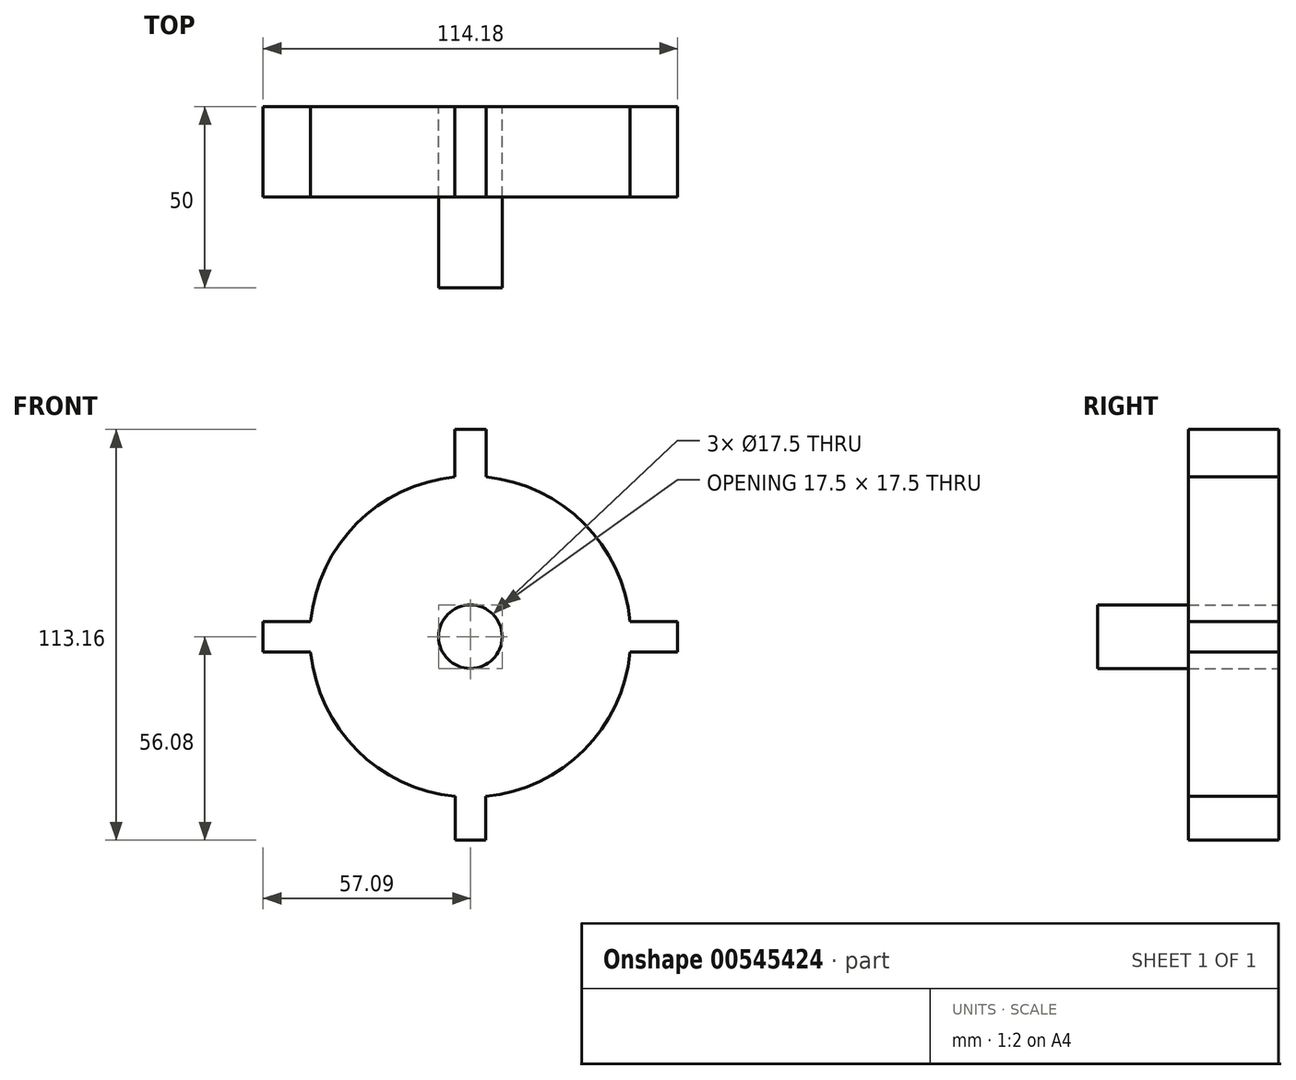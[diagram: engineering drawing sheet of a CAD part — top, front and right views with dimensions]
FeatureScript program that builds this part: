
annotation { "Feature Type Name" : "Feature", "Feature Type Description" : "" }
export const myFeature = defineFeature(function(context is Context, id is Id, definition is map)
    precondition{}
    {
        {
            var Q0;
            Q0=qCreatedBy(makeId("Front.planeOp"),FACE);
            var sketch = newSketch(context, id + "F0", { "sketchPlane" : qUnion([Q0])});
            skLineSegment(sketch, "E0.top", {"start": v(4.3, 57.08) * mm, "end": v(-4.3, 57.08) * mm});
            skLineSegment(sketch, "E0.left", {"start": v(4.3, 44) * mm, "end": v(4.3, 57.08) * mm});
            skLineSegment(sketch, "E0.right", {"start": v(-4.3, 44) * mm, "end": v(-4.3, 57.08) * mm});
            skPoint(sketch, "E0.middle", {"position": v(0, 50.54) * mm});
            skLineSegment(sketch, "E1.1.1", {"start": v(-44, -4.2) * mm, "end": v(-57.09, -4.2) * mm});
            skLineSegment(sketch, "E1.1.2", {"start": v(-57.09, 4.2) * mm, "end": v(-57.09, -4.2) * mm});
            skLineSegment(sketch, "E1.1.3", {"start": v(-44, 4.2) * mm, "end": v(-57.09, 4.2) * mm});
            skLineSegment(sketch, "E1.2.1", {"start": v(4.2, -43) * mm, "end": v(4.2, -56.08) * mm});
            skLineSegment(sketch, "E1.2.2", {"start": v(-4.2, -56.08) * mm, "end": v(4.2, -56.08) * mm});
            skLineSegment(sketch, "E1.2.3", {"start": v(-4.2, -43) * mm, "end": v(-4.2, -56.08) * mm});
            skLineSegment(sketch, "E1.3.1", {"start": v(44, 4.2) * mm, "end": v(57.09, 4.2) * mm});
            skLineSegment(sketch, "E1.3.2", {"start": v(57.09, -4.2) * mm, "end": v(57.09, 4.2) * mm});
            skLineSegment(sketch, "E1.3.3", {"start": v(44, -4.2) * mm, "end": v(57.09, -4.2) * mm});
            skPoint(sketch, "E1.center", {"position": v(0, 0) * mm});
            skArc(sketch, "E2", {"start": v(-4.3, 44) * mm, "mid": v(-31.3, 31.23) * mm, "end": v(-44, 4.2) * mm});
            skArc(sketch, "E3.trimOffspring", {"start": v(44, 4.2) * mm, "mid": v(31.3, 31.23) * mm, "end": v(4.3, 44) * mm});
            skArc(sketch, "E4.trimOffspring", {"start": v(4.2, -44) * mm, "mid": v(31.26, -31.26) * mm, "end": v(44, -4.2) * mm});
            skArc(sketch, "E5.trimOffspring", {"start": v(-44, -4.2) * mm, "mid": v(-31.26, -31.26) * mm, "end": v(-4.2, -44) * mm});
            skSolve(sketch);
        }
        {
            var Q0;
            Q0=makeQuery(id+"F0.imprint","IMPRINT",FACE,{"disambiguationData":[TD([[makeQuery(id+"F0.imprint","IMPRINT",EDGE,{"derivedFrom":sQuery(id+"F0.wireOp",EDGE,"E0.top")}),1.0]])]});
            extrude(context, id + "F1", {"entities" : qUnion([Q0]), "depth" : 25 * mm, "offsetDistance" : 25 * mm});
        }
        {
            var Q0;
            Q0=sQuery(id+"F0.wireOp",VERTEX,"E1.center");
            var Q1;
            Q1=makeQuery(id+"F1.opExtrude","SWEPT_BODY",BODY,{"disambiguationData":[OSD([sQuery(id+"F0.wireOp",EDGE,"E0.top"),sQuery(id+"F0.wireOp",EDGE,"E0.left"),sQuery(id+"F0.wireOp",EDGE,"E0.right"),sQuery(id+"F0.wireOp",EDGE,"E1.1.1"),sQuery(id+"F0.wireOp",EDGE,"E1.1.2"),sQuery(id+"F0.wireOp",EDGE,"E1.1.3"),sQuery(id+"F0.wireOp",EDGE,"E1.2.1"),sQuery(id+"F0.wireOp",EDGE,"E1.2.2"),sQuery(id+"F0.wireOp",EDGE,"E1.2.3"),sQuery(id+"F0.wireOp",EDGE,"E1.3.1"),sQuery(id+"F0.wireOp",EDGE,"E1.3.2"),sQuery(id+"F0.wireOp",EDGE,"E1.3.3"),sQuery(id+"F0.wireOp",EDGE,"E2"),sQuery(id+"F0.wireOp",EDGE,"E3.trimOffspring"),sQuery(id+"F0.wireOp",EDGE,"E4.trimOffspring"),sQuery(id+"F0.wireOp",EDGE,"E5.trimOffspring")])]});
            hole(context, id + "F2", {"style" : HoleStyle.SIMPLE, "endStyle" : HoleEndStyle.THROUGH, "oppositeDirection" : true, "standardTappedOrClearance" : lookupTablePath({ "standard" : "ISO", "engagement" : "75%", "pitch" : "2.5 mm", "size" : "M20", "type" : "Tapped" }), "standardBlindInLast" : lookupTablePath({ "standard" : "ISO", "engagement" : "75%", "pitch" : "2.5 mm", "size" : "M20", "type" : "Tapped" }), "holeDiameter" : 17.5 * mm, "showTappedDepth" : true, "tappedDepth" : 5 * mm, "tapClearance" : 0, "locations" : qUnion([Q0]), "scope" : qUnion([Q1]), "majorDiameter" : 20 * mm});
        }
        {
            var Q0;
            Q0=makeQuery(id+"F1.opExtrude","CAP_FACE",FACE,{"disambiguationData":[OSD([sQuery(id+"F0.wireOp",EDGE,"E0.top"),sQuery(id+"F0.wireOp",EDGE,"E0.left"),sQuery(id+"F0.wireOp",EDGE,"E0.right"),sQuery(id+"F0.wireOp",EDGE,"E1.1.1"),sQuery(id+"F0.wireOp",EDGE,"E1.1.2"),sQuery(id+"F0.wireOp",EDGE,"E1.1.3"),sQuery(id+"F0.wireOp",EDGE,"E1.2.1"),sQuery(id+"F0.wireOp",EDGE,"E1.2.2"),sQuery(id+"F0.wireOp",EDGE,"E1.2.3"),sQuery(id+"F0.wireOp",EDGE,"E1.3.1"),sQuery(id+"F0.wireOp",EDGE,"E1.3.2"),sQuery(id+"F0.wireOp",EDGE,"E1.3.3"),sQuery(id+"F0.wireOp",EDGE,"E2"),sQuery(id+"F0.wireOp",EDGE,"E3.trimOffspring"),sQuery(id+"F0.wireOp",EDGE,"E4.trimOffspring"),sQuery(id+"F0.wireOp",EDGE,"E5.trimOffspring")])],"isStart":false});
            var sketch = newSketch(context, id + "F3", { "sketchPlane" : qUnion([Q0])});
            skCircle(sketch, "E6", {"center": v(0, 0) * mm, "radius": 8.75 * mm});
            skSolve(sketch);
        }
        {
            var Q0;
            Q0 = qSketchRegion(id + "F3", true);
            extrude(context, id + "F4", {"entities" : qUnion([Q0]), "depth" : 25 * mm, "offsetDistance" : 25 * mm});
        }
    });
